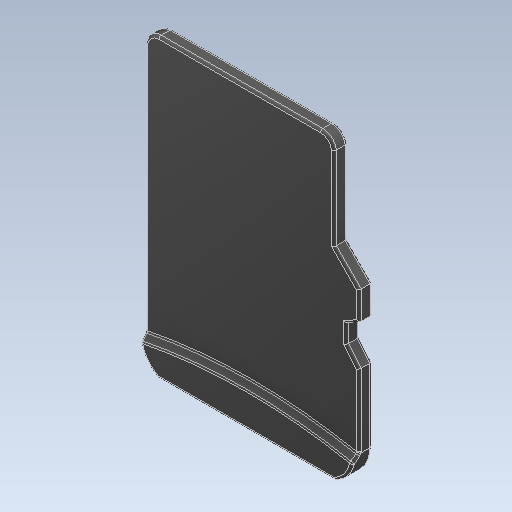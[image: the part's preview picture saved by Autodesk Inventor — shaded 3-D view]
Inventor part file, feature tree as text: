
AUTODESK INVENTOR PART (.ipt)
format: ipt  version: 2021 (Build 250183000, 183)  size: 172,544 bytes
history: native  units: in
note: dims shown in document units (in); Inventor stores cm internally (conversion verified against a paired STEP export)
features: fillet x1
ambient origin geometry x8: Origin, YZ Plane, XZ Plane, XY Plane, X Axis, Y Axis, Z Axis, Center Point
bodies: Solid1 (feature_tree)
feature tree (1):
  fillet  "Fillet2"  [1 undecoded]
note: 1 required parameter value undecoded (feature->parameter linkage not recoverable at this tier; creation-order binding heuristic only, values carry confidence <= 0.55)
